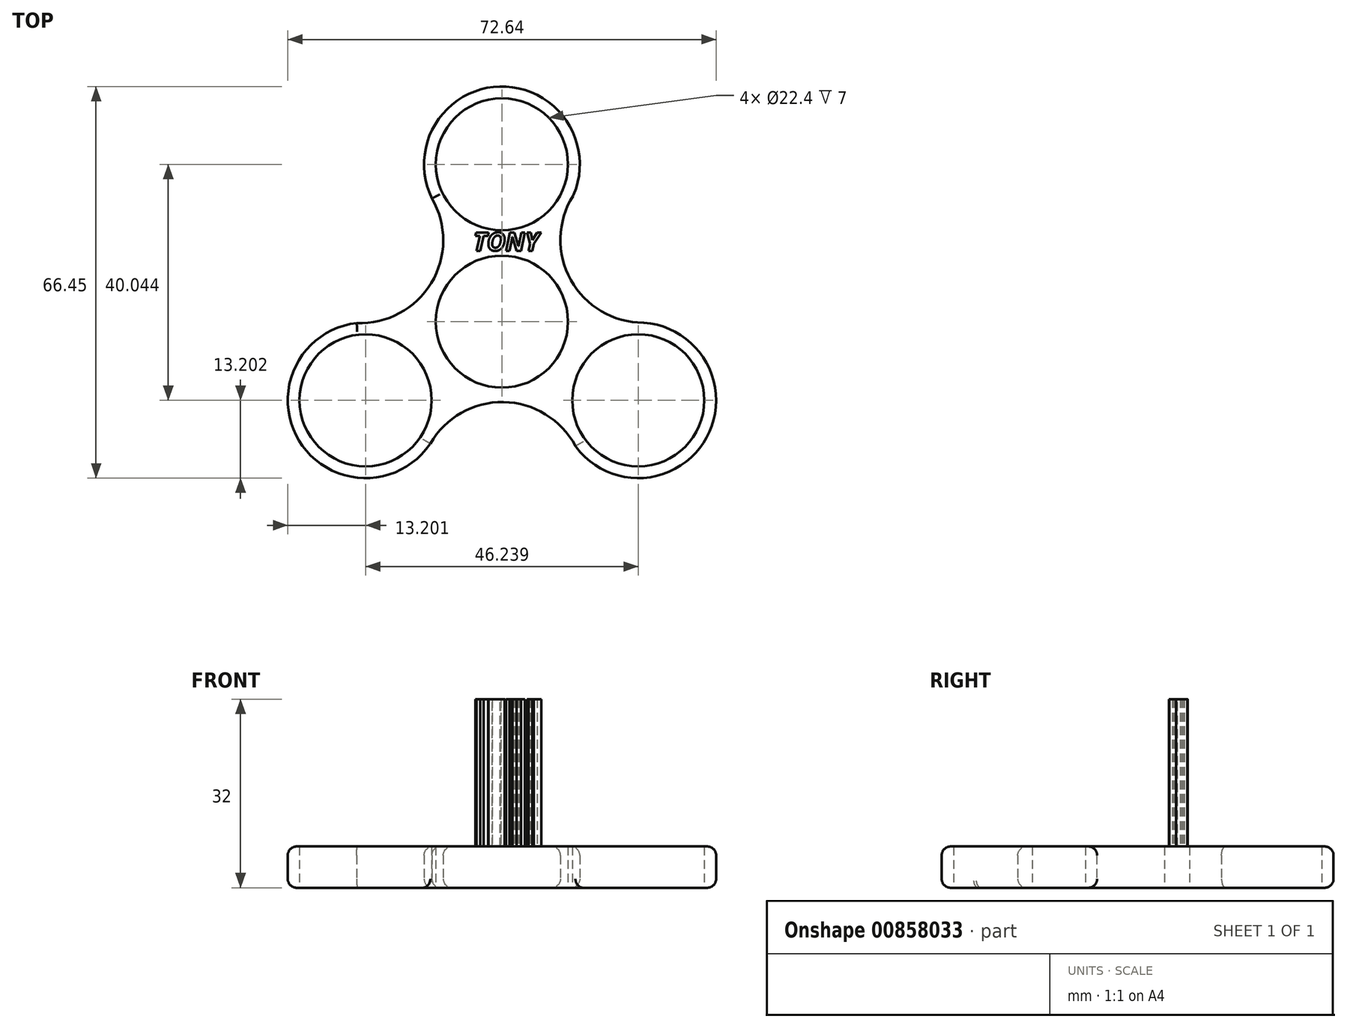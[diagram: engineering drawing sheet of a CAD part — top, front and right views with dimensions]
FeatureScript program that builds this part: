
annotation { "Feature Type Name" : "Feature", "Feature Type Description" : "" }
export const myFeature = defineFeature(function(context is Context, id is Id, definition is map)
    precondition{}
    {
        {
            var Q0;
            Q0=qCreatedBy(makeId("Top.planeOp"),FACE);
            var sketch = newSketch(context, id + "F0", { "sketchPlane" : qUnion([Q0])});
            skCircle(sketch, "E0", {"center": v(0, 0) * mm, "radius": 11.2 * mm});
            skCircle(sketch, "E1", {"center": v(0, 26.7) * mm, "radius": 11.2 * mm});
            skArc(sketch, "E2", {"start": v(11.11, 19.57) * mm, "mid": v(0.27, 39.9) * mm, "end": v(-11.4, 20.03) * mm});
            skArc(sketch, "E3.1.0", {"start": v(-22.5, -0.16) * mm, "mid": v(-34.68, -19.71) * mm, "end": v(-11.65, -19.89) * mm});
            skCircle(sketch, "E3.1.1", {"center": v(-23.12, -13.35) * mm, "radius": 11.2 * mm});
            skArc(sketch, "E3.2.0", {"start": v(11.4, -19.4) * mm, "mid": v(34.41, -20.18) * mm, "end": v(23.05, -0.15) * mm});
            skCircle(sketch, "E3.2.1", {"center": v(23.12, -13.35) * mm, "radius": 11.2 * mm});
            skArc(sketch, "E4", {"start": v(12.1, 21.43) * mm, "mid": v(11.67, 7.1) * mm, "end": v(24.03, -0.18) * mm});
            skArc(sketch, "E5.1.0", {"start": v(-24.61, -0.23) * mm, "mid": v(-11.98, 6.56) * mm, "end": v(-11.86, 20.9) * mm});
            skArc(sketch, "E5.2.0", {"start": v(12.5, -21.2) * mm, "mid": v(0.3, -13.65) * mm, "end": v(-12.17, -20.72) * mm});
            skSolve(sketch);
        }
        {
            var Q0;
            Q0=makeQuery(id+"F0.imprint","IMPRINT",FACE,{"disambiguationData":[TD([[makeQuery(id+"F0.imprint","IMPRINT",EDGE,{"derivedFrom":sQuery(id+"F0.wireOp",EDGE,"E0")}),-1.0]])]});
            extrude(context, id + "F1", {"entities" : qUnion([Q0]), "depth" : 7 * mm, "offsetDistance" : 25 * mm});
        }
        {
            var Q0;
            Q0=makeQuery(id+"F1.opExtrude","CAP_EDGE",EDGE,{"disambiguationData":[OSD([sQuery(id+"F0.wireOp",EDGE,"E5.2.0")])],"isStart":true});
            fillet(context, id + "F2", {"entities" : qUnion([Q0]), "radius" : 1.5 * mm, "tangentPropagation" : true, "allowEdgeOverflow" : false});
        }
        {
            var Q0;
            Q0=makeQuery(id+"F1.opExtrude","SWEPT_FACE",FACE,{"disambiguationData":[OSD([sQuery(id+"F0.wireOp",EDGE,"E4")])]});
            var Q1;
            Q1=makeQuery(id+"F1.opExtrude","CAP_EDGE",EDGE,{"disambiguationData":[OSD([sQuery(id+"F0.wireOp",EDGE,"E4")])],"isStart":true});
            var Q2;
            Q2=makeQuery(id+"F1.opExtrude","CAP_EDGE",EDGE,{"disambiguationData":[OSD([sQuery(id+"F0.wireOp",EDGE,"E3.2.0")])],"isStart":false});
            var Q3;
            Q3=makeQuery(id+"F1.opExtrude","CAP_EDGE",EDGE,{"disambiguationData":[OSD([sQuery(id+"F0.wireOp",EDGE,"E5.2.0")])],"isStart":false});
            var Q4;
            Q4=makeQuery(id+"F1.opExtrude","CAP_EDGE",EDGE,{"disambiguationData":[OSD([sQuery(id+"F0.wireOp",EDGE,"E3.1.0")])],"isStart":false});
            var Q5;
            Q5=makeQuery(id+"F1.opExtrude","CAP_EDGE",EDGE,{"disambiguationData":[OSD([sQuery(id+"F0.wireOp",EDGE,"E5.1.0")])],"isStart":false});
            var Q6;
            Q6=makeQuery(id+"F1.opExtrude","CAP_EDGE",EDGE,{"disambiguationData":[OSD([sQuery(id+"F0.wireOp",EDGE,"E2")])],"isStart":false});
            fillet(context, id + "F3", {"entities" : qUnion([Q0, Q1, Q2, Q3, Q4, Q5, Q6]), "radius" : 1.5 * mm, "tangentPropagation" : true, "allowEdgeOverflow" : false});
        }
        {
            var Q0;
            Q0=makeQuery(id+"F1.opExtrude","CAP_EDGE",EDGE,{"disambiguationData":[OSD([sQuery(id+"F0.wireOp",EDGE,"E2")])],"isStart":true});
            var Q1;
            Q1=makeQuery(id+"F1.opExtrude","CAP_EDGE",EDGE,{"disambiguationData":[OSD([sQuery(id+"F0.wireOp",EDGE,"E5.1.0")])],"isStart":true});
            var Q2;
            Q2=makeQuery(id+"F1.opExtrude","CAP_EDGE",EDGE,{"disambiguationData":[OSD([sQuery(id+"F0.wireOp",EDGE,"E3.1.0")])],"isStart":true});
            var Q3;
            {var subQ0=sQuery(id+"F0.wireOp",EDGE,"E5.2.0");Q3=makeQuery(id+"F2.opFillet","BLEND_EDGE",EDGE,{"blendedFrom":[makeQuery(id+"F1.opExtrude","CAP_EDGE",EDGE,{"disambiguationData":[OSD([subQ0])],"isStart":true}),makeQuery(id+"F1.opExtrude","CAP_FACE",FACE,{"disambiguationData":[OSD([sQuery(id+"F0.wireOp",EDGE,"E0"),sQuery(id+"F0.wireOp",EDGE,"E1"),sQuery(id+"F0.wireOp",EDGE,"E2"),sQuery(id+"F0.wireOp",EDGE,"E3.1.0"),sQuery(id+"F0.wireOp",EDGE,"E3.1.1"),sQuery(id+"F0.wireOp",EDGE,"E3.2.0"),sQuery(id+"F0.wireOp",EDGE,"E3.2.1"),sQuery(id+"F0.wireOp",EDGE,"E4"),sQuery(id+"F0.wireOp",EDGE,"E5.1.0"),subQ0])],"isStart":true})],"blendedInto":[makeQuery(id+"F1.opExtrude","CAP_FACE",FACE,{"disambiguationData":[OSD([sQuery(id+"F0.wireOp",EDGE,"E0"),sQuery(id+"F0.wireOp",EDGE,"E1"),sQuery(id+"F0.wireOp",EDGE,"E2"),sQuery(id+"F0.wireOp",EDGE,"E3.1.0"),sQuery(id+"F0.wireOp",EDGE,"E3.1.1"),sQuery(id+"F0.wireOp",EDGE,"E3.2.0"),sQuery(id+"F0.wireOp",EDGE,"E3.2.1"),sQuery(id+"F0.wireOp",EDGE,"E4"),sQuery(id+"F0.wireOp",EDGE,"E5.1.0"),subQ0])],"isStart":true})]});}
            var Q4;
            Q4=makeQuery(id+"F1.opExtrude","CAP_EDGE",EDGE,{"disambiguationData":[OSD([sQuery(id+"F0.wireOp",EDGE,"E3.2.0")])],"isStart":true});
            var Q5;
            {var subQ0=sQuery(id+"F0.wireOp",EDGE,"E4");Q5=makeQuery(id+"F3.opFillet","BLEND_EDGE",EDGE,{"blendedFrom":[makeQuery(id+"F1.opExtrude","CAP_EDGE",EDGE,{"disambiguationData":[OSD([subQ0])],"isStart":true}),makeQuery(id+"F1.opExtrude","CAP_FACE",FACE,{"disambiguationData":[OSD([sQuery(id+"F0.wireOp",EDGE,"E0"),sQuery(id+"F0.wireOp",EDGE,"E1"),sQuery(id+"F0.wireOp",EDGE,"E2"),sQuery(id+"F0.wireOp",EDGE,"E3.1.0"),sQuery(id+"F0.wireOp",EDGE,"E3.1.1"),sQuery(id+"F0.wireOp",EDGE,"E3.2.0"),sQuery(id+"F0.wireOp",EDGE,"E3.2.1"),subQ0,sQuery(id+"F0.wireOp",EDGE,"E5.1.0"),sQuery(id+"F0.wireOp",EDGE,"E5.2.0")])],"isStart":true})],"blendedInto":[makeQuery(id+"F1.opExtrude","CAP_FACE",FACE,{"disambiguationData":[OSD([sQuery(id+"F0.wireOp",EDGE,"E0"),sQuery(id+"F0.wireOp",EDGE,"E1"),sQuery(id+"F0.wireOp",EDGE,"E2"),sQuery(id+"F0.wireOp",EDGE,"E3.1.0"),sQuery(id+"F0.wireOp",EDGE,"E3.1.1"),sQuery(id+"F0.wireOp",EDGE,"E3.2.0"),sQuery(id+"F0.wireOp",EDGE,"E3.2.1"),subQ0,sQuery(id+"F0.wireOp",EDGE,"E5.1.0"),sQuery(id+"F0.wireOp",EDGE,"E5.2.0")])],"isStart":true})]});}
            fillet(context, id + "F4", {"entities" : qUnion([Q0, Q1, Q2, Q3, Q4, Q5]), "radius" : 1.5 * mm, "tangentPropagation" : true, "allowEdgeOverflow" : false});
        }
        {
            var Q0;
            Q0=makeQuery(id+"F1.opExtrude","CAP_FACE",FACE,{"disambiguationData":[OSD([sQuery(id+"F0.wireOp",EDGE,"E0"),sQuery(id+"F0.wireOp",EDGE,"E1"),sQuery(id+"F0.wireOp",EDGE,"E2"),sQuery(id+"F0.wireOp",EDGE,"E3.1.0"),sQuery(id+"F0.wireOp",EDGE,"E3.1.1"),sQuery(id+"F0.wireOp",EDGE,"E3.2.0"),sQuery(id+"F0.wireOp",EDGE,"E3.2.1"),sQuery(id+"F0.wireOp",EDGE,"E4"),sQuery(id+"F0.wireOp",EDGE,"E5.1.0"),sQuery(id+"F0.wireOp",EDGE,"E5.2.0")])],"isStart":false});
            var sketch = newSketch(context, id + "F5", { "sketchPlane" : qUnion([Q0])});
            skText(sketch, "E6", { "text": "TONY", "fontName": "OpenSans-BoldItalic.ttf"});
            const initialGuessF5  = {"E6": [-0.00485, 0.01203, 1, 0, 0.00311]};
            skSetInitialGuess(sketch, initialGuessF5);
            skSolve(sketch);
        }
        {
            var Q0;
            Q0 = qSketchRegion(id + "F5", true);
            extrude(context, id + "F6", {"entities" : qUnion([Q0]), "operationType" : NewBodyOperationType.ADD, "depth" : 25 * mm, "offsetDistance" : 25 * mm});
        }
    });
